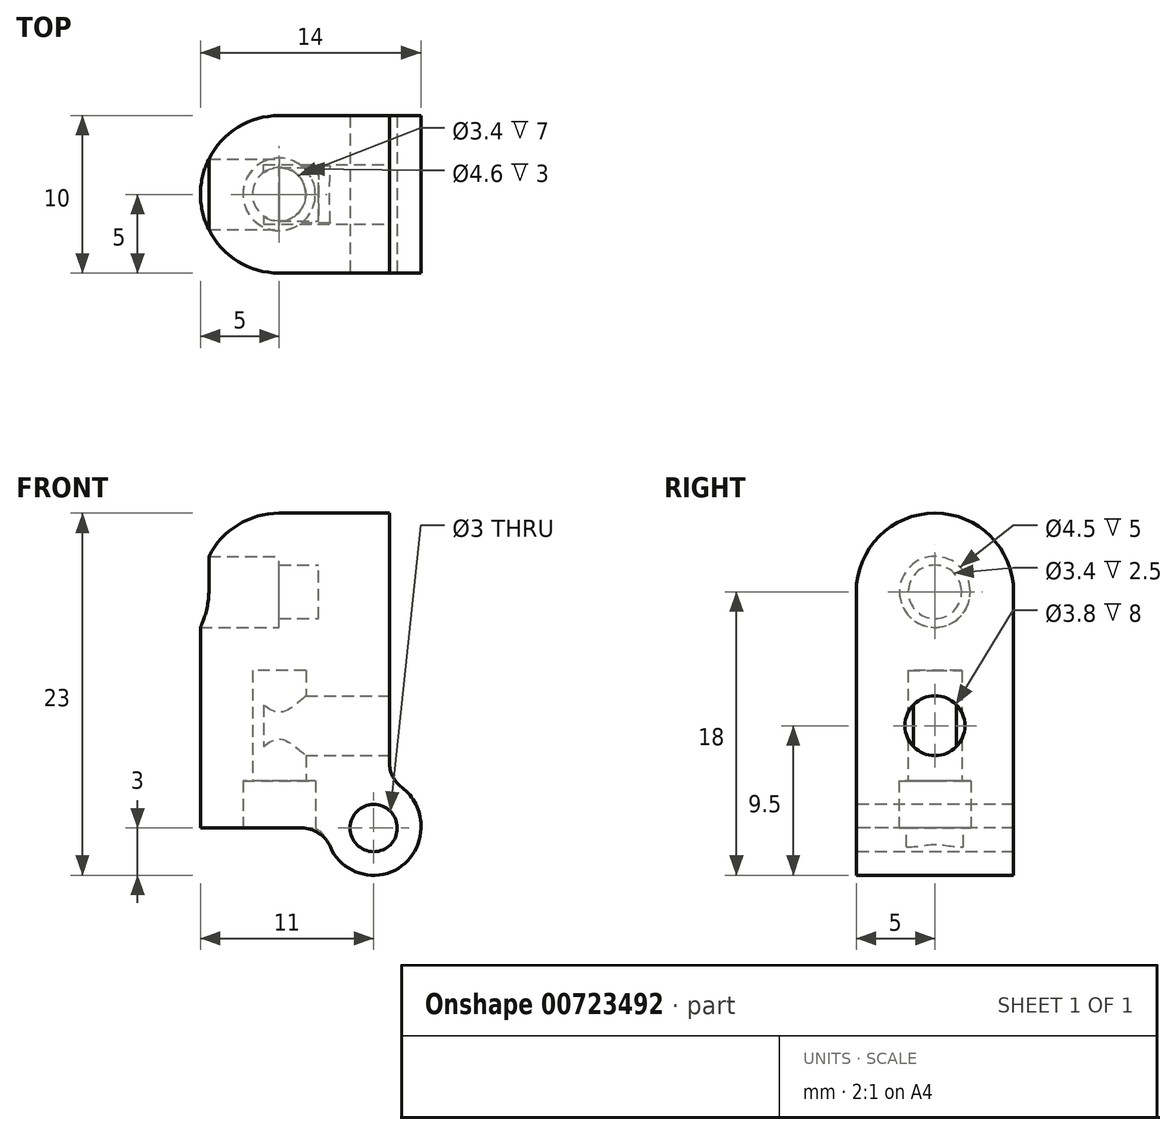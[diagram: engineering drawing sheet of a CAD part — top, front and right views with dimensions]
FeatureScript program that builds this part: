
annotation { "Feature Type Name" : "Feature", "Feature Type Description" : "" }
export const myFeature = defineFeature(function(context is Context, id is Id, definition is map)
    precondition{}
    {
        {
            var Q0;
            Q0=qCreatedBy(makeId("Top.planeOp"),FACE);
            var sketch = newSketch(context, id + "F0", { "sketchPlane" : qUnion([Q0])});
            skArc(sketch, "E0", {"start": v(0, 5) * mm, "mid": v(-5, 0) * mm, "end": v(0, -5) * mm});
            skCircle(sketch, "E1", {"center": v(0, 0) * mm, "radius": 2.3 * mm});
            skLineSegment(sketch, "E2", {"start": v(0, 5) * mm, "end": v(7, 5) * mm});
            skLineSegment(sketch, "E3", {"start": v(7, 5) * mm, "end": v(7, -5) * mm});
            skLineSegment(sketch, "E4", {"start": v(7, -5) * mm, "end": v(0, -5) * mm});
            skSolve(sketch);
        }
        {
            var Q0;
            Q0 = qSketchRegion(id + "F0", true);
            extrude(context, id + "F1", {"entities" : qUnion([Q0]), "depth" : 3 * mm, "offsetDistance" : 25 * mm});
        }
        {
            var Q0;
            Q0=makeQuery(id+"F1.opExtrude","CAP_FACE",FACE,{"disambiguationData":[OSD([sQuery(id+"F0.wireOp",EDGE,"E0"),sQuery(id+"F0.wireOp",EDGE,"E1")])],"isStart":false});
            var sketch = newSketch(context, id + "F2", { "sketchPlane" : qUnion([Q0])});
            skCircle(sketch, "E5", {"center": v(0, 0) * mm, "radius": 1.7 * mm});
            skLineSegment(sketch, "E6", {"start": v(0, -5) * mm, "end": v(7, -5) * mm});
            skLineSegment(sketch, "E7", {"start": v(7, -5) * mm, "end": v(7, 5) * mm});
            skLineSegment(sketch, "E8", {"start": v(7, 5) * mm, "end": v(0, 5) * mm});
            skArc(sketch, "E9", {"start": v(0, 5) * mm, "mid": v(-5, 0) * mm, "end": v(0, -5) * mm});
            skSolve(sketch);
        }
        {
            var Q0;
            Q0 = qSketchRegion(id + "F2", true);
            extrude(context, id + "F3", {"entities" : qUnion([Q0]), "operationType" : NewBodyOperationType.ADD, "depth" : 7 * mm, "offsetDistance" : 25 * mm});
        }
        {
            var Q0;
            Q0=makeQuery(id+"F3.opExtrude","CAP_FACE",FACE,{"disambiguationData":[OSD([sQuery(id+"F2.wireOp",EDGE,"E5"),sQuery(id+"F2.wireOp",EDGE,"E6"),sQuery(id+"F2.wireOp",EDGE,"E7"),sQuery(id+"F2.wireOp",EDGE,"E8"),sQuery(id+"F2.wireOp",EDGE,"E9")])],"isStart":false});
            var sketch = newSketch(context, id + "F4", { "sketchPlane" : qUnion([Q0])});
            skLineSegment(sketch, "E10", {"start": v(0, 5) * mm, "end": v(7, 5) * mm});
            skLineSegment(sketch, "E11", {"start": v(7, 5) * mm, "end": v(7, -5) * mm});
            skLineSegment(sketch, "E12", {"start": v(7, -5) * mm, "end": v(0, -5) * mm});
            skArc(sketch, "E13", {"start": v(0, 5) * mm, "mid": v(-5, 0) * mm, "end": v(0, -5) * mm});
            skSolve(sketch);
        }
        {
            var Q0;
            Q0 = qSketchRegion(id + "F4", true);
            extrude(context, id + "F5", {"entities" : qUnion([Q0]), "operationType" : NewBodyOperationType.ADD, "depth" : 10 * mm, "offsetDistance" : 25 * mm});
        }
        {
            var Q0;
            Q0=qCreatedBy(makeId("Right.planeOp"),FACE);
            cPlane(context, id + "F6", {"entities" : qUnion([Q0]), "cplaneType" : CPlaneType.OFFSET, "offset" : 2.5 * mm, "width" : 150 * mm, "height" : 150 * mm});
        }
        {
            var Q0;
            Q0=qCreatedBy(id+"F6.planeOp",FACE);
            var sketch = newSketch(context, id + "F7", { "sketchPlane" : qUnion([Q0])});
            skCircle(sketch, "E14", {"center": v(0, 15) * mm, "radius": 1.7 * mm});
            skSolve(sketch);
        }
        {
            var Q0;
            Q0 = qSketchRegion(id + "F7", true);
            extrude(context, id + "F8", {"entities" : qUnion([Q0]), "operationType" : NewBodyOperationType.REMOVE, "endBound" : BoundingType.THROUGH_ALL, "oppositeDirection" : true, "depth" : 25 * mm, "offsetDistance" : 25 * mm});
        }
        {
            var Q0;
            Q0=qCreatedBy(makeId("Right.planeOp"),FACE);
            var sketch = newSketch(context, id + "F9", { "sketchPlane" : qUnion([Q0])});
            skCircle(sketch, "E15", {"center": v(0, 15) * mm, "radius": 2.25 * mm});
            skSolve(sketch);
        }
        {
            var Q0;
            Q0 = qSketchRegion(id + "F9", true);
            extrude(context, id + "F10", {"entities" : qUnion([Q0]), "operationType" : NewBodyOperationType.REMOVE, "oppositeDirection" : true, "depth" : 25 * mm, "offsetDistance" : 25 * mm});
        }
        {
            var Q0;
            Q0=makeQuery(id+"F5.boolean.opBoolean","MERGE",FACE,{"derivedFrom":[makeQuery(id+"F3.boolean.opBoolean","MERGE",FACE,{"derivedFrom":[makeQuery(id+"F1.opExtrude","SWEPT_FACE",FACE,{"disambiguationData":[OSD([sQuery(id+"F0.wireOp",EDGE,"E3")])]}),makeQuery(id+"F3.opExtrude","SWEPT_FACE",FACE,{"disambiguationData":[OSD([sQuery(id+"F2.wireOp",EDGE,"E7")])]})]}),makeQuery(id+"F5.opExtrude","SWEPT_FACE",FACE,{"disambiguationData":[OSD([sQuery(id+"F4.wireOp",EDGE,"E11")])]})]});
            var sketch = newSketch(context, id + "F11", { "sketchPlane" : qUnion([Q0])});
            skCircle(sketch, "E16", {"center": v(0, 6.5) * mm, "radius": 1.9 * mm});
            skSolve(sketch);
        }
        {
            var Q0;
            Q0 = qSketchRegion(id + "F11", true);
            extrude(context, id + "F12", {"entities" : qUnion([Q0]), "operationType" : NewBodyOperationType.REMOVE, "oppositeDirection" : true, "depth" : 8 * mm, "offsetDistance" : 25 * mm});
        }
        {
            var Q0;
            Q0=makeQuery(id+"F5.opExtrude","CAP_EDGE",EDGE,{"disambiguationData":[OSD([sQuery(id+"F4.wireOp",EDGE,"E10")])],"isStart":false});
            fillet(context, id + "F13", {"entities" : qUnion([Q0]), "radius" : 5 * mm, "tangentPropagation" : true, "allowEdgeOverflow" : false});
        }
        {
            var Q0;
            Q0=makeQuery(id+"F5.boolean.opBoolean","MERGE",FACE,{"derivedFrom":[makeQuery(id+"F3.boolean.opBoolean","MERGE",FACE,{"derivedFrom":[makeQuery(id+"F1.opExtrude","SWEPT_FACE",FACE,{"disambiguationData":[OSD([sQuery(id+"F0.wireOp",EDGE,"E4")])]}),makeQuery(id+"F3.opExtrude","SWEPT_FACE",FACE,{"disambiguationData":[OSD([sQuery(id+"F2.wireOp",EDGE,"E6")])]})]}),makeQuery(id+"F5.opExtrude","SWEPT_FACE",FACE,{"disambiguationData":[OSD([sQuery(id+"F4.wireOp",EDGE,"E12")])]})]});
            var sketch = newSketch(context, id + "F14", { "sketchPlane" : qUnion([Q0])});
            skPoint(sketch, "E17.centerSnap0", {"position": v(2.98, 0) * mm});
            skPoint(sketch, "E17.center.orphan", {"position": v(2.98, 0) * mm});
            skLineSegment(sketch, "E18", {"start": v(3, 0) * mm, "end": v(7, 0) * mm});
            skLineSegment(sketch, "E19", {"start": v(9, 0) * mm, "end": v(9, -3) * mm});
            skLineSegment(sketch, "E20", {"start": v(9, -3) * mm, "end": v(3, -3) * mm});
            skLineSegment(sketch, "E21", {"start": v(3, -3) * mm, "end": v(3, 0) * mm});
            skLineSegment(sketch, "E22", {"start": v(9, 0) * mm, "end": v(9, 3) * mm});
            skLineSegment(sketch, "E23", {"start": v(9, 3) * mm, "end": v(7, 3) * mm});
            skLineSegment(sketch, "E24", {"start": v(7, 3) * mm, "end": v(7, 0) * mm});
            skSolve(sketch);
        }
        {
            var Q0;
            Q0 = qSketchRegion(id + "F14", true);
            var Q1;
            Q1=makeQuery(id+"F5.boolean.opBoolean","MERGE",FACE,{"derivedFrom":[makeQuery(id+"F3.boolean.opBoolean","MERGE",FACE,{"derivedFrom":[makeQuery(id+"F1.opExtrude","SWEPT_FACE",FACE,{"disambiguationData":[OSD([sQuery(id+"F0.wireOp",EDGE,"E2")])]}),makeQuery(id+"F3.opExtrude","SWEPT_FACE",FACE,{"disambiguationData":[OSD([sQuery(id+"F2.wireOp",EDGE,"E8")])]})]}),makeQuery(id+"F5.opExtrude","SWEPT_FACE",FACE,{"disambiguationData":[OSD([sQuery(id+"F4.wireOp",EDGE,"E10")])]})]});
            extrude(context, id + "F15", {"entities" : qUnion([Q0]), "operationType" : NewBodyOperationType.ADD, "endBound" : BoundingType.UP_TO_SURFACE, "oppositeDirection" : true, "depth" : 25 * mm, "endBoundEntityFace" : qUnion([Q1]), "offsetDistance" : 25 * mm});
        }
        {
            var Q0;
            Q0=makeQuery(id+"F15.boolean.opBoolean","MERGE",FACE,{"derivedFrom":[makeQuery(id+"F5.boolean.opBoolean","MERGE",FACE,{"derivedFrom":[makeQuery(id+"F3.boolean.opBoolean","MERGE",FACE,{"derivedFrom":[makeQuery(id+"F1.opExtrude","SWEPT_FACE",FACE,{"disambiguationData":[OSD([sQuery(id+"F0.wireOp",EDGE,"E4")])]}),makeQuery(id+"F3.opExtrude","SWEPT_FACE",FACE,{"disambiguationData":[OSD([sQuery(id+"F2.wireOp",EDGE,"E6")])]})]}),makeQuery(id+"F5.opExtrude","SWEPT_FACE",FACE,{"disambiguationData":[OSD([sQuery(id+"F4.wireOp",EDGE,"E12")])]})]}),makeQuery(id+"F15.opExtrude","CAP_FACE",FACE,{"disambiguationData":[OSD([sQuery(id+"F14.wireOp",EDGE,"Jhcn7PWy-kaLP-zIgq-bvvw-evDGIhWy2E3e.bottom"),sQuery(id+"F14.wireOp",EDGE,"Jhcn7PWy-kaLP-zIgq-bvvw-evDGIhWy2E3e.top"),sQuery(id+"F14.wireOp",EDGE,"Jhcn7PWy-kaLP-zIgq-bvvw-evDGIhWy2E3e.left"),sQuery(id+"F14.wireOp",EDGE,"Jhcn7PWy-kaLP-zIgq-bvvw-evDGIhWy2E3e.right")])],"isStart":true})]});
            var sketch = newSketch(context, id + "F16", { "sketchPlane" : qUnion([Q0])});
            skCircle(sketch, "E25", {"center": v(6, 0) * mm, "radius": 1.5 * mm});
            skSolve(sketch);
        }
        {
            var Q0;
            Q0 = qSketchRegion(id + "F16", true);
            extrude(context, id + "F17", {"entities" : qUnion([Q0]), "operationType" : NewBodyOperationType.REMOVE, "endBound" : BoundingType.THROUGH_ALL, "oppositeDirection" : true, "depth" : 25 * mm, "offsetDistance" : 25 * mm});
        }
        {
            var Q0;
            Q0=makeQuery(id+"F15.opExtrude","SWEPT_EDGE",EDGE,{"disambiguationData":[OSD([sQuery(id+"F14.wireOp",EDGE,"E20"),sQuery(id+"F14.wireOp",EDGE,"E21")])]});
            var Q1;
            Q1=makeQuery(id+"F15.opExtrude","SWEPT_EDGE",EDGE,{"disambiguationData":[OSD([sQuery(id+"F14.wireOp",EDGE,"E19"),sQuery(id+"F14.wireOp",EDGE,"E20")])]});
            var Q2;
            Q2=makeQuery(id+"F15.opExtrude","SWEPT_EDGE",EDGE,{"disambiguationData":[OSD([sQuery(id+"F14.wireOp",EDGE,"E22"),sQuery(id+"F14.wireOp",EDGE,"E23")])]});
            fillet(context, id + "F18", {"entities" : qUnion([Q0, Q1, Q2]), "radius" : 3 * mm, "tangentPropagation" : true, "allowEdgeOverflow" : false});
        }
        {
            var Q0;
            Q0=makeQuery(id+"F18.opFillet","BLEND_EDGE",EDGE,{"blendedFrom":[makeQuery(id+"F15.opExtrude","SWEPT_EDGE",EDGE,{"disambiguationData":[OSD([sQuery(id+"F14.wireOp",EDGE,"E22"),sQuery(id+"F14.wireOp",EDGE,"E23")])]}),makeQuery(id+"F5.boolean.opBoolean","MERGE",FACE,{"derivedFrom":[makeQuery(id+"F3.boolean.opBoolean","MERGE",FACE,{"derivedFrom":[makeQuery(id+"F1.opExtrude","SWEPT_FACE",FACE,{"disambiguationData":[OSD([sQuery(id+"F0.wireOp",EDGE,"E3")])]}),makeQuery(id+"F3.opExtrude","SWEPT_FACE",FACE,{"disambiguationData":[OSD([sQuery(id+"F2.wireOp",EDGE,"E7")])]})]}),makeQuery(id+"F5.opExtrude","SWEPT_FACE",FACE,{"disambiguationData":[OSD([sQuery(id+"F4.wireOp",EDGE,"E11")])]})]})],"blendedInto":[makeQuery(id+"F5.boolean.opBoolean","MERGE",FACE,{"derivedFrom":[makeQuery(id+"F3.boolean.opBoolean","MERGE",FACE,{"derivedFrom":[makeQuery(id+"F1.opExtrude","SWEPT_FACE",FACE,{"disambiguationData":[OSD([sQuery(id+"F0.wireOp",EDGE,"E3")])]}),makeQuery(id+"F3.opExtrude","SWEPT_FACE",FACE,{"disambiguationData":[OSD([sQuery(id+"F2.wireOp",EDGE,"E7")])]})]}),makeQuery(id+"F5.opExtrude","SWEPT_FACE",FACE,{"disambiguationData":[OSD([sQuery(id+"F4.wireOp",EDGE,"E11")])]})]})]});
            var Q1;
            Q1=makeQuery(id+"F18.opFillet","BLEND_EDGE",EDGE,{"blendedFrom":[makeQuery(id+"F15.opExtrude","SWEPT_EDGE",EDGE,{"disambiguationData":[OSD([sQuery(id+"F14.wireOp",EDGE,"E20"),sQuery(id+"F14.wireOp",EDGE,"E21")])]}),makeQuery(id+"F1.opExtrude","CAP_FACE",FACE,{"disambiguationData":[OSD([sQuery(id+"F0.wireOp",EDGE,"E0"),sQuery(id+"F0.wireOp",EDGE,"E1"),sQuery(id+"F0.wireOp",EDGE,"E2"),sQuery(id+"F0.wireOp",EDGE,"E3"),sQuery(id+"F0.wireOp",EDGE,"E4")])],"isStart":true})],"blendedInto":[makeQuery(id+"F1.opExtrude","CAP_FACE",FACE,{"disambiguationData":[OSD([sQuery(id+"F0.wireOp",EDGE,"E0"),sQuery(id+"F0.wireOp",EDGE,"E1"),sQuery(id+"F0.wireOp",EDGE,"E2"),sQuery(id+"F0.wireOp",EDGE,"E3"),sQuery(id+"F0.wireOp",EDGE,"E4")])],"isStart":true})]});
            fillet(context, id + "F19", {"entities" : qUnion([Q0, Q1]), "radius" : 2 * mm, "tangentPropagation" : true, "allowEdgeOverflow" : false});
        }
    });
